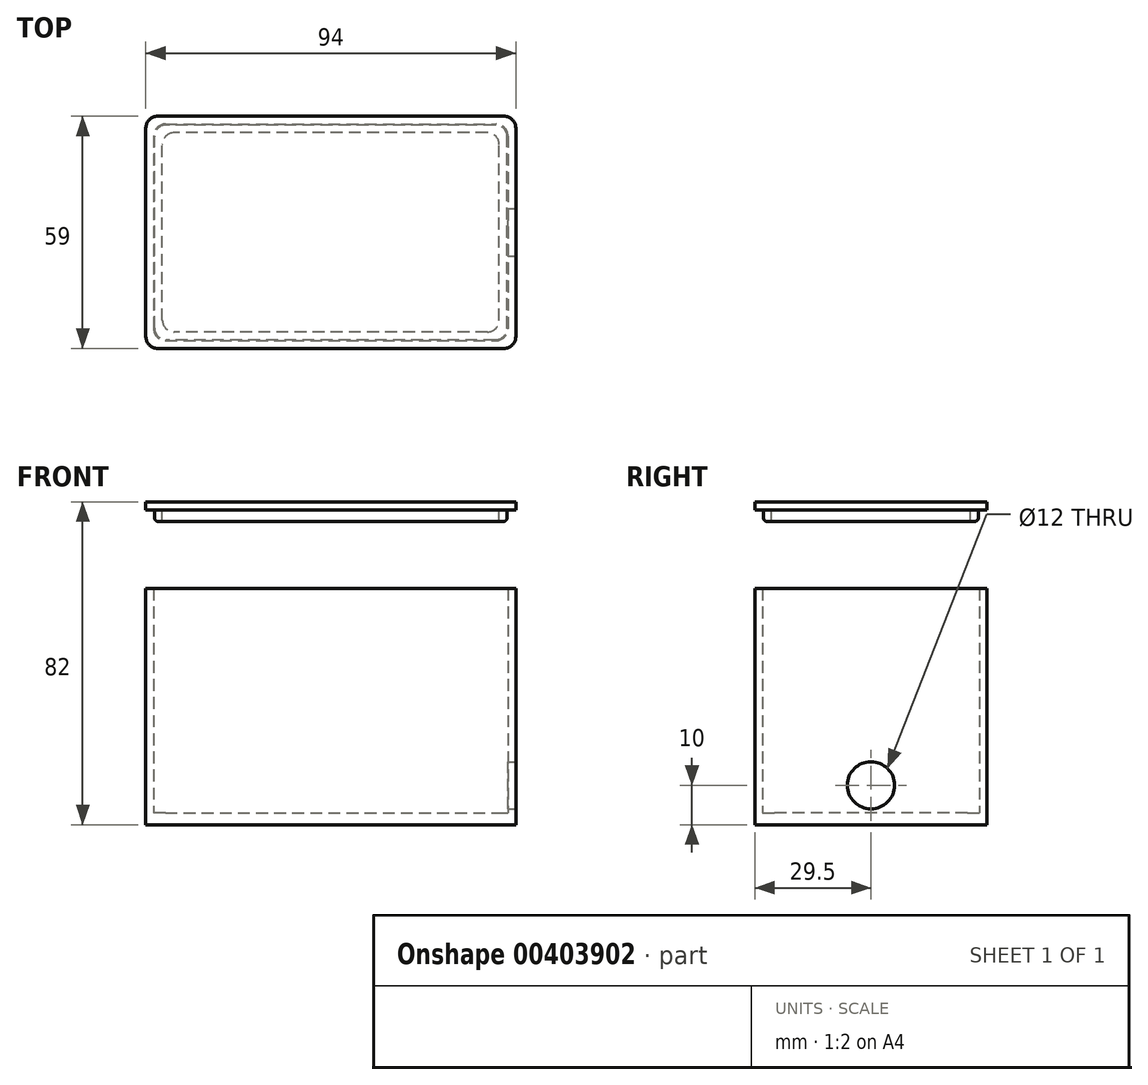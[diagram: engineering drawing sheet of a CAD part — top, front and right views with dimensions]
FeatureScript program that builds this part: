
annotation { "Feature Type Name" : "Feature", "Feature Type Description" : "" }
export const myFeature = defineFeature(function(context is Context, id is Id, definition is map)
    precondition{}
    {
        {
            var Q0;
            Q0=qCreatedBy(makeId("Top.planeOp"),FACE);
            var sketch = newSketch(context, id + "F0", { "sketchPlane" : qUnion([Q0])});
            skLineSegment(sketch, "E0.bottom", {"start": v(-45, 27.5) * mm, "end": v(45, 27.5) * mm});
            skLineSegment(sketch, "E0.top", {"start": v(-45, -27.5) * mm, "end": v(45, -27.5) * mm});
            skLineSegment(sketch, "E0.left", {"start": v(-45, 27.5) * mm, "end": v(-45, -27.5) * mm});
            skLineSegment(sketch, "E0.right", {"start": v(45, 27.5) * mm, "end": v(45, -27.5) * mm});
            skLineSegment(sketch, "E1.0", {"start": v(-47, 29.5) * mm, "end": v(-47, -29.5) * mm});
            skLineSegment(sketch, "E1.1", {"start": v(-47, 29.5) * mm, "end": v(47, 29.5) * mm});
            skLineSegment(sketch, "E1.2", {"start": v(47, 29.5) * mm, "end": v(47, -29.5) * mm});
            skLineSegment(sketch, "E1.3", {"start": v(-47, -29.5) * mm, "end": v(47, -29.5) * mm});
            skSolve(sketch);
        }
        {
            var Q0;
            Q0=makeQuery(id+"F0.imprint","IMPRINT",FACE,{"disambiguationData":[TD([[makeQuery(id+"F0.imprint","IMPRINT",EDGE,{"derivedFrom":sQuery(id+"F0.wireOp",EDGE,"E0.bottom")}),1.0]])]});
            extrude(context, id + "F1", {"entities" : qUnion([Q0]), "depth" : 60 * mm});
        }
        {
            var Q0;
            Q0=makeQuery(id+"F0.imprint","IMPRINT",FACE,{"disambiguationData":[TD([[makeQuery(id+"F0.imprint","IMPRINT",EDGE,{"derivedFrom":sQuery(id+"F0.wireOp",EDGE,"E0.bottom")}),-1.0]])]});
            extrude(context, id + "F2", {"entities" : qUnion([Q0]), "operationType" : NewBodyOperationType.ADD, "depth" : 3 * mm});
        }
        {
            var Q0;
            Q0=makeQuery(id+"F1.opExtrude","SWEPT_FACE",FACE,{"disambiguationData":[OSD([sQuery(id+"F0.wireOp",EDGE,"E1.2")])]});
            var sketch = newSketch(context, id + "F3", { "sketchPlane" : qUnion([Q0])});
            skCircle(sketch, "E2", {"center": v(0, 10) * mm, "radius": 6 * mm});
            skSolve(sketch);
        }
        {
            var Q0;
            Q0=makeQuery(id+"F3.imprint","IMPRINT",FACE,{"disambiguationData":[TD([[makeQuery(id+"F3.imprint","IMPRINT",EDGE,{"derivedFrom":sQuery(id+"F3.wireOp",EDGE,"E2")}),1.0]])]});
            extrude(context, id + "F4", {"entities" : qUnion([Q0]), "operationType" : NewBodyOperationType.REMOVE, "oppositeDirection" : true, "depth" : 5 * mm});
        }
        {
            var Q0;
            Q0=makeQuery(id+"F1.opExtrude","SWEPT_EDGE",EDGE,{"disambiguationData":[OSD([sQuery(id+"F0.wireOp",EDGE,"E1.2"),sQuery(id+"F0.wireOp",EDGE,"E1.3")])]});
            var Q1;
            Q1=makeQuery(id+"F1.opExtrude","SWEPT_EDGE",EDGE,{"disambiguationData":[OSD([sQuery(id+"F0.wireOp",EDGE,"E1.1"),sQuery(id+"F0.wireOp",EDGE,"E1.2")])]});
            var Q2;
            Q2=makeQuery(id+"F1.opExtrude","SWEPT_EDGE",EDGE,{"disambiguationData":[OSD([sQuery(id+"F0.wireOp",EDGE,"E1.0"),sQuery(id+"F0.wireOp",EDGE,"E1.1")])]});
            var Q3;
            Q3=makeQuery(id+"F1.opExtrude","SWEPT_EDGE",EDGE,{"disambiguationData":[OSD([sQuery(id+"F0.wireOp",EDGE,"E1.0"),sQuery(id+"F0.wireOp",EDGE,"E1.3")])]});
            var Q4;
            Q4=makeQuery(id+"F1.opExtrude","SWEPT_EDGE",EDGE,{"disambiguationData":[OSD([sQuery(id+"F0.wireOp",EDGE,"E0.bottom"),sQuery(id+"F0.wireOp",EDGE,"E0.left")])]});
            var Q5;
            Q5=makeQuery(id+"F1.opExtrude","SWEPT_EDGE",EDGE,{"disambiguationData":[OSD([sQuery(id+"F0.wireOp",EDGE,"E0.top"),sQuery(id+"F0.wireOp",EDGE,"E0.left")])]});
            var Q6;
            Q6=makeQuery(id+"F1.opExtrude","SWEPT_EDGE",EDGE,{"disambiguationData":[OSD([sQuery(id+"F0.wireOp",EDGE,"E0.bottom"),sQuery(id+"F0.wireOp",EDGE,"E0.right")])]});
            var Q7;
            Q7=makeQuery(id+"F1.opExtrude","SWEPT_EDGE",EDGE,{"disambiguationData":[OSD([sQuery(id+"F0.wireOp",EDGE,"E0.top"),sQuery(id+"F0.wireOp",EDGE,"E0.right")])]});
            fillet(context, id + "F5", {"entities" : qUnion([Q0, Q1, Q2, Q3, Q4, Q5, Q6, Q7]), "radius" : 3 * mm, "tangentPropagation" : true, "allowEdgeOverflow" : false});
        }
        {
            var Q0;
            Q0=qCreatedBy(makeId("Top.planeOp"),FACE);
            cPlane(context, id + "F6", {"entities" : qUnion([Q0]), "cplaneType" : CPlaneType.OFFSET, "offset" : 80 * mm, "width" : 150 * mm, "height" : 150 * mm});
        }
        {
            var Q0;
            Q0=qCreatedBy(id+"F6.planeOp",FACE);
            var sketch = newSketch(context, id + "F7", { "sketchPlane" : qUnion([Q0])});
            skLineSegment(sketch, "E3.bottom", {"start": v(-45, 27.5) * mm, "end": v(45, 27.5) * mm});
            skLineSegment(sketch, "E3.top", {"start": v(-45, -27.5) * mm, "end": v(45, -27.5) * mm});
            skLineSegment(sketch, "E3.left", {"start": v(-45, 27.5) * mm, "end": v(-45, -27.5) * mm});
            skLineSegment(sketch, "E3.right", {"start": v(45, 27.5) * mm, "end": v(45, -27.5) * mm});
            skLineSegment(sketch, "E4.0", {"start": v(-47, 29.5) * mm, "end": v(47, 29.5) * mm});
            skLineSegment(sketch, "E4.1", {"start": v(-47, 29.5) * mm, "end": v(-47, -29.5) * mm});
            skLineSegment(sketch, "E4.2", {"start": v(-47, -29.5) * mm, "end": v(47, -29.5) * mm});
            skLineSegment(sketch, "E4.3", {"start": v(47, 29.5) * mm, "end": v(47, -29.5) * mm});
            skSolve(sketch);
        }
        {
            var Q0;
            Q0=makeQuery(id+"F7.imprint","IMPRINT",FACE,{"disambiguationData":[TD([[makeQuery(id+"F7.imprint","IMPRINT",EDGE,{"derivedFrom":sQuery(id+"F7.wireOp",EDGE,"E3.bottom")}),1.0]])]});
            var Q1;
            Q1=makeQuery(id+"F7.imprint","IMPRINT",FACE,{"disambiguationData":[TD([[makeQuery(id+"F7.imprint","IMPRINT",EDGE,{"derivedFrom":sQuery(id+"F7.wireOp",EDGE,"E3.bottom")}),-1.0]])]});
            extrude(context, id + "F8", {"entities" : qUnion([Q0, Q1]), "depth" : 2 * mm});
        }
        {
            var Q0;
            Q0=makeQuery(id+"F8.opExtrude","SWEPT_EDGE",EDGE,{"disambiguationData":[OSD([sQuery(id+"F7.wireOp",EDGE,"E4.0"),sQuery(id+"F7.wireOp",EDGE,"E4.1")])]});
            var Q1;
            Q1=makeQuery(id+"F8.opExtrude","SWEPT_EDGE",EDGE,{"disambiguationData":[OSD([sQuery(id+"F7.wireOp",EDGE,"E4.1"),sQuery(id+"F7.wireOp",EDGE,"E4.2")])]});
            var Q2;
            Q2=makeQuery(id+"F8.opExtrude","SWEPT_EDGE",EDGE,{"disambiguationData":[OSD([sQuery(id+"F7.wireOp",EDGE,"E4.2"),sQuery(id+"F7.wireOp",EDGE,"E4.3")])]});
            var Q3;
            Q3=makeQuery(id+"F8.opExtrude","SWEPT_EDGE",EDGE,{"disambiguationData":[OSD([sQuery(id+"F7.wireOp",EDGE,"E4.0"),sQuery(id+"F7.wireOp",EDGE,"E4.3")])]});
            fillet(context, id + "F9", {"entities" : qUnion([Q0, Q1, Q2, Q3]), "radius" : 3 * mm, "tangentPropagation" : true, "allowEdgeOverflow" : false});
        }
        {
            var Q0;
            Q0=makeQuery(id+"F8.opExtrude","CAP_FACE",FACE,{"disambiguationData":[OSD([sQuery(id+"F7.wireOp",EDGE,"E4.0"),sQuery(id+"F7.wireOp",EDGE,"E4.1"),sQuery(id+"F7.wireOp",EDGE,"E4.2"),sQuery(id+"F7.wireOp",EDGE,"E4.3")])],"isStart":true});
            var sketch = newSketch(context, id + "F10", { "sketchPlane" : qUnion([Q0])});
            skLineSegment(sketch, "E5.bottom", {"start": v(44.8, 27.3) * mm, "end": v(-44.8, 27.3) * mm});
            skLineSegment(sketch, "E5.top", {"start": v(44.8, -27.3) * mm, "end": v(-44.8, -27.3) * mm});
            skLineSegment(sketch, "E5.left", {"start": v(44.8, 27.3) * mm, "end": v(44.8, -27.3) * mm});
            skLineSegment(sketch, "E5.right", {"start": v(-44.8, 27.3) * mm, "end": v(-44.8, -27.3) * mm});
            skLineSegment(sketch, "E6.bottom", {"start": v(42.8, 25.3) * mm, "end": v(-42.8, 25.3) * mm});
            skLineSegment(sketch, "E6.top", {"start": v(42.8, -25.3) * mm, "end": v(-42.8, -25.3) * mm});
            skLineSegment(sketch, "E6.left", {"start": v(42.8, 25.3) * mm, "end": v(42.8, -25.3) * mm});
            skLineSegment(sketch, "E6.right", {"start": v(-42.8, 25.3) * mm, "end": v(-42.8, -25.3) * mm});
            skSolve(sketch);
        }
        {
            var Q0;
            Q0=makeQuery(id+"F10.imprint","IMPRINT",FACE,{"disambiguationData":[TD([[makeQuery(id+"F10.imprint","IMPRINT",EDGE,{"derivedFrom":sQuery(id+"F10.wireOp",EDGE,"E5.bottom")}),1.0]])]});
            extrude(context, id + "F11", {"entities" : qUnion([Q0]), "operationType" : NewBodyOperationType.ADD, "depth" : 3 * mm});
        }
        {
            var Q0;
            Q0=makeQuery(id+"F11.opExtrude","SWEPT_EDGE",EDGE,{"disambiguationData":[OSD([sQuery(id+"F10.wireOp",EDGE,"E5.bottom"),sQuery(id+"F10.wireOp",EDGE,"E5.left")])]});
            var Q1;
            Q1=makeQuery(id+"F11.opExtrude","SWEPT_EDGE",EDGE,{"disambiguationData":[OSD([sQuery(id+"F10.wireOp",EDGE,"E5.bottom"),sQuery(id+"F10.wireOp",EDGE,"E5.right")])]});
            var Q2;
            Q2=makeQuery(id+"F11.opExtrude","SWEPT_EDGE",EDGE,{"disambiguationData":[OSD([sQuery(id+"F10.wireOp",EDGE,"E6.bottom"),sQuery(id+"F10.wireOp",EDGE,"E6.left")])]});
            var Q3;
            Q3=makeQuery(id+"F11.opExtrude","SWEPT_EDGE",EDGE,{"disambiguationData":[OSD([sQuery(id+"F10.wireOp",EDGE,"E5.top"),sQuery(id+"F10.wireOp",EDGE,"E5.left")])]});
            var Q4;
            Q4=makeQuery(id+"F11.opExtrude","SWEPT_EDGE",EDGE,{"disambiguationData":[OSD([sQuery(id+"F10.wireOp",EDGE,"E6.bottom"),sQuery(id+"F10.wireOp",EDGE,"E6.right")])]});
            var Q5;
            Q5=makeQuery(id+"F11.opExtrude","SWEPT_EDGE",EDGE,{"disambiguationData":[OSD([sQuery(id+"F10.wireOp",EDGE,"E5.top"),sQuery(id+"F10.wireOp",EDGE,"E5.right")])]});
            var Q6;
            Q6=makeQuery(id+"F11.opExtrude","SWEPT_EDGE",EDGE,{"disambiguationData":[OSD([sQuery(id+"F10.wireOp",EDGE,"E6.top"),sQuery(id+"F10.wireOp",EDGE,"E6.left")])]});
            var Q7;
            Q7=makeQuery(id+"F11.opExtrude","SWEPT_EDGE",EDGE,{"disambiguationData":[OSD([sQuery(id+"F10.wireOp",EDGE,"E6.top"),sQuery(id+"F10.wireOp",EDGE,"E6.right")])]});
            fillet(context, id + "F12", {"entities" : qUnion([Q0, Q1, Q2, Q3, Q4, Q5, Q6, Q7]), "radius" : 3 * mm, "tangentPropagation" : true, "allowEdgeOverflow" : false});
        }
        {
            var Q0;
            Q0=makeQuery(id+"F11.opExtrude","CAP_EDGE",EDGE,{"disambiguationData":[OSD([sQuery(id+"F10.wireOp",EDGE,"E5.top")])],"isStart":false});
            var Q1;
            {var subQ0=sQuery(id+"F10.wireOp",EDGE,"E5.right");var subQ1=sQuery(id+"F10.wireOp",EDGE,"E5.top");Q1=makeQuery(id+"F12.opFillet","BLEND_EDGE",EDGE,{"blendedFrom":[makeQuery(id+"F11.opExtrude","SWEPT_EDGE",EDGE,{"disambiguationData":[OSD([subQ1,subQ0])]}),makeQuery(id+"F11.opExtrude","CAP_FACE",FACE,{"disambiguationData":[OSD([sQuery(id+"F10.wireOp",EDGE,"E5.bottom"),subQ1,sQuery(id+"F10.wireOp",EDGE,"E5.left"),subQ0,sQuery(id+"F10.wireOp",EDGE,"E6.bottom"),sQuery(id+"F10.wireOp",EDGE,"E6.top"),sQuery(id+"F10.wireOp",EDGE,"E6.left"),sQuery(id+"F10.wireOp",EDGE,"E6.right")])],"isStart":false})],"blendedInto":[makeQuery(id+"F11.opExtrude","CAP_FACE",FACE,{"disambiguationData":[OSD([sQuery(id+"F10.wireOp",EDGE,"E5.bottom"),subQ1,sQuery(id+"F10.wireOp",EDGE,"E5.left"),subQ0,sQuery(id+"F10.wireOp",EDGE,"E6.bottom"),sQuery(id+"F10.wireOp",EDGE,"E6.top"),sQuery(id+"F10.wireOp",EDGE,"E6.left"),sQuery(id+"F10.wireOp",EDGE,"E6.right")])],"isStart":false})]});}
            var Q2;
            Q2=makeQuery(id+"F11.opExtrude","CAP_EDGE",EDGE,{"disambiguationData":[OSD([sQuery(id+"F10.wireOp",EDGE,"E5.right")])],"isStart":false});
            var Q3;
            {var subQ0=sQuery(id+"F10.wireOp",EDGE,"E5.right");var subQ1=sQuery(id+"F10.wireOp",EDGE,"E5.bottom");Q3=makeQuery(id+"F12.opFillet","BLEND_EDGE",EDGE,{"blendedFrom":[makeQuery(id+"F11.opExtrude","SWEPT_EDGE",EDGE,{"disambiguationData":[OSD([subQ1,subQ0])]}),makeQuery(id+"F11.opExtrude","CAP_FACE",FACE,{"disambiguationData":[OSD([subQ1,sQuery(id+"F10.wireOp",EDGE,"E5.top"),sQuery(id+"F10.wireOp",EDGE,"E5.left"),subQ0,sQuery(id+"F10.wireOp",EDGE,"E6.bottom"),sQuery(id+"F10.wireOp",EDGE,"E6.top"),sQuery(id+"F10.wireOp",EDGE,"E6.left"),sQuery(id+"F10.wireOp",EDGE,"E6.right")])],"isStart":false})],"blendedInto":[makeQuery(id+"F11.opExtrude","CAP_FACE",FACE,{"disambiguationData":[OSD([subQ1,sQuery(id+"F10.wireOp",EDGE,"E5.top"),sQuery(id+"F10.wireOp",EDGE,"E5.left"),subQ0,sQuery(id+"F10.wireOp",EDGE,"E6.bottom"),sQuery(id+"F10.wireOp",EDGE,"E6.top"),sQuery(id+"F10.wireOp",EDGE,"E6.left"),sQuery(id+"F10.wireOp",EDGE,"E6.right")])],"isStart":false})]});}
            var Q4;
            Q4=makeQuery(id+"F11.opExtrude","CAP_EDGE",EDGE,{"disambiguationData":[OSD([sQuery(id+"F10.wireOp",EDGE,"E5.bottom")])],"isStart":false});
            var Q5;
            Q5=makeQuery(id+"F11.opExtrude","CAP_EDGE",EDGE,{"disambiguationData":[OSD([sQuery(id+"F10.wireOp",EDGE,"E5.left")])],"isStart":false});
            var Q6;
            {var subQ0=sQuery(id+"F10.wireOp",EDGE,"E5.left");var subQ1=sQuery(id+"F10.wireOp",EDGE,"E5.bottom");Q6=makeQuery(id+"F12.opFillet","BLEND_EDGE",EDGE,{"blendedFrom":[makeQuery(id+"F11.opExtrude","SWEPT_EDGE",EDGE,{"disambiguationData":[OSD([subQ1,subQ0])]}),makeQuery(id+"F11.opExtrude","CAP_FACE",FACE,{"disambiguationData":[OSD([subQ1,sQuery(id+"F10.wireOp",EDGE,"E5.top"),subQ0,sQuery(id+"F10.wireOp",EDGE,"E5.right"),sQuery(id+"F10.wireOp",EDGE,"E6.bottom"),sQuery(id+"F10.wireOp",EDGE,"E6.top"),sQuery(id+"F10.wireOp",EDGE,"E6.left"),sQuery(id+"F10.wireOp",EDGE,"E6.right")])],"isStart":false})],"blendedInto":[makeQuery(id+"F11.opExtrude","CAP_FACE",FACE,{"disambiguationData":[OSD([subQ1,sQuery(id+"F10.wireOp",EDGE,"E5.top"),subQ0,sQuery(id+"F10.wireOp",EDGE,"E5.right"),sQuery(id+"F10.wireOp",EDGE,"E6.bottom"),sQuery(id+"F10.wireOp",EDGE,"E6.top"),sQuery(id+"F10.wireOp",EDGE,"E6.left"),sQuery(id+"F10.wireOp",EDGE,"E6.right")])],"isStart":false})]});}
            var Q7;
            {var subQ0=sQuery(id+"F10.wireOp",EDGE,"E5.left");var subQ1=sQuery(id+"F10.wireOp",EDGE,"E5.top");Q7=makeQuery(id+"F12.opFillet","BLEND_EDGE",EDGE,{"blendedFrom":[makeQuery(id+"F11.opExtrude","SWEPT_EDGE",EDGE,{"disambiguationData":[OSD([subQ1,subQ0])]}),makeQuery(id+"F11.opExtrude","CAP_FACE",FACE,{"disambiguationData":[OSD([sQuery(id+"F10.wireOp",EDGE,"E5.bottom"),subQ1,subQ0,sQuery(id+"F10.wireOp",EDGE,"E5.right"),sQuery(id+"F10.wireOp",EDGE,"E6.bottom"),sQuery(id+"F10.wireOp",EDGE,"E6.top"),sQuery(id+"F10.wireOp",EDGE,"E6.left"),sQuery(id+"F10.wireOp",EDGE,"E6.right")])],"isStart":false})],"blendedInto":[makeQuery(id+"F11.opExtrude","CAP_FACE",FACE,{"disambiguationData":[OSD([sQuery(id+"F10.wireOp",EDGE,"E5.bottom"),subQ1,subQ0,sQuery(id+"F10.wireOp",EDGE,"E5.right"),sQuery(id+"F10.wireOp",EDGE,"E6.bottom"),sQuery(id+"F10.wireOp",EDGE,"E6.top"),sQuery(id+"F10.wireOp",EDGE,"E6.left"),sQuery(id+"F10.wireOp",EDGE,"E6.right")])],"isStart":false})]});}
            fillet(context, id + "F13", {"entities" : qUnion([Q0, Q1, Q2, Q3, Q4, Q5, Q6, Q7]), "radius" : 1 * mm, "tangentPropagation" : true, "allowEdgeOverflow" : false});
        }
    });
